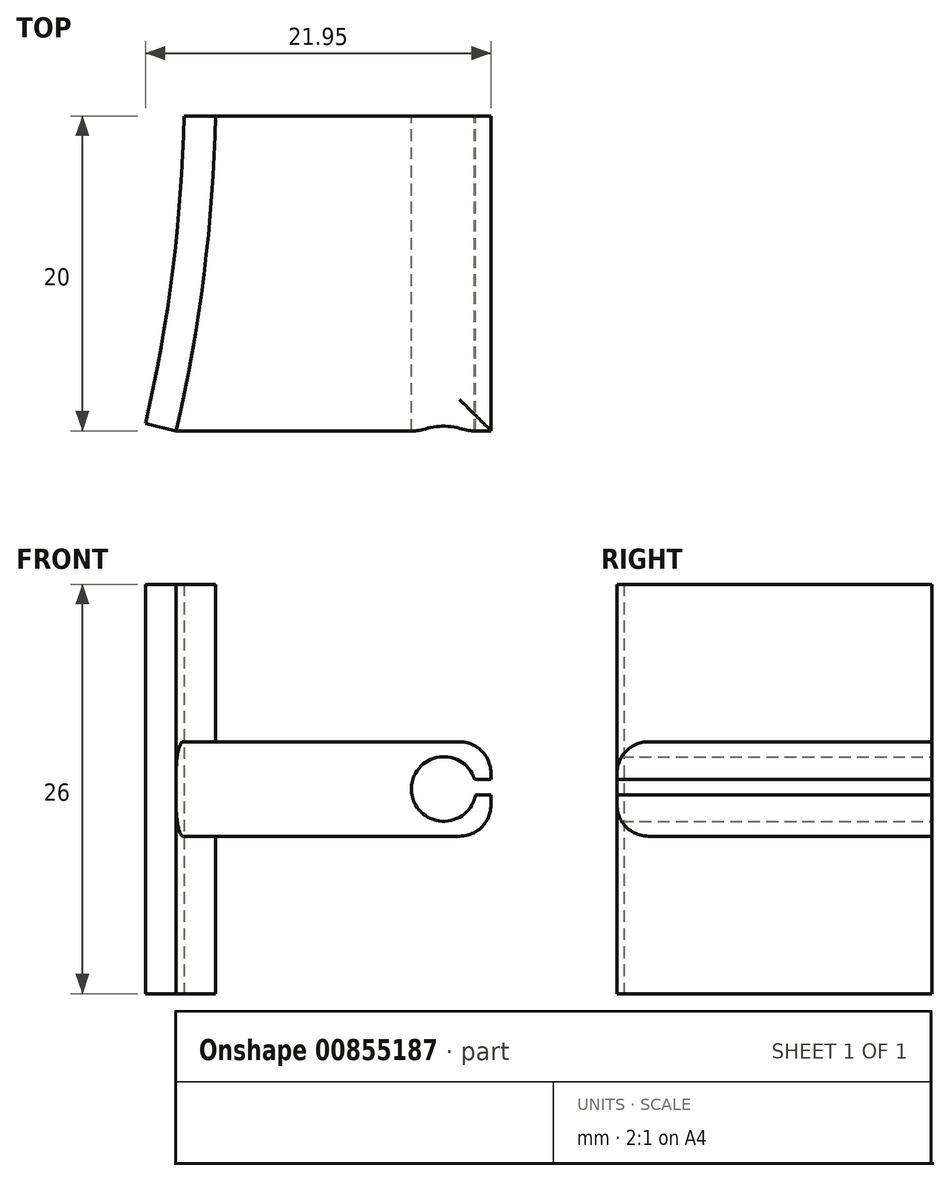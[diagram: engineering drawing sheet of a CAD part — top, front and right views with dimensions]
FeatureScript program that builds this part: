
annotation { "Feature Type Name" : "Feature", "Feature Type Description" : "" }
export const myFeature = defineFeature(function(context is Context, id is Id, definition is map)
    precondition{}
    {
        {
            var Q0;
            Q0=qCreatedBy(makeId("Top.planeOp"),FACE);
            var sketch = newSketch(context, id + "F0", { "sketchPlane" : qUnion([Q0])});
            skLineSegment(sketch, "E0.bottom", {"start": v(10, 10) * mm, "end": v(-9.5, 10) * mm});
            skLineSegment(sketch, "E0.top", {"start": v(10, -10) * mm, "end": v(-10, -10) * mm});
            skLineSegment(sketch, "E0.left", {"start": v(10, 10) * mm, "end": v(10, -10) * mm});
            skPoint(sketch, "E0.middle", {"position": v(0, 0) * mm});
            skArc(sketch, "E1", {"start": v(-10, -10) * mm, "mid": v(-8.23, -0.07) * mm, "end": v(-7.5, 10) * mm});
            skArc(sketch, "E2.0", {"start": v(-11.95, -9.55) * mm, "mid": v(-10.21, 0.18) * mm, "end": v(-9.5, 10.04) * mm});
            skPoint(sketch, "E3.orphan", {"position": v(-10, 10) * mm});
            skLineSegment(sketch, "E4", {"start": v(-11.95, -9.55) * mm, "end": v(-10, -10) * mm});
            skSolve(sketch);
        }
        {
            var Q0;
            {var subQ3=sQuery(id+"F0.wireOp",EDGE,"E1");Q0=makeQuery(id+"F0.imprint","IMPRINT",FACE,{"disambiguationData":[TD([[makeQuery(id+"F0.imprint","IMPRINT",EDGE,{"derivedFrom":subQ3}),1.0]])]});}
            extrude(context, id + "F1", {"entities" : qUnion([Q0]), "depth" : 16 * mm, "offsetDistance" : 25 * mm, "hasSecondDirection" : true, "secondDirectionOppositeDirection" : true, "secondDirectionDepth" : 10 * mm});
        }
        {
            var Q0;
            Q0=makeQuery(id+"F0.imprint","IMPRINT",FACE,{"disambiguationData":[TD([[makeQuery(id+"F0.imprint","IMPRINT",EDGE,{"derivedFrom":sQuery(id+"F0.wireOp",EDGE,"E0.top")}),-1.0]])]});
            extrude(context, id + "F2", {"entities" : qUnion([Q0]), "operationType" : NewBodyOperationType.ADD, "depth" : 6 * mm, "offsetDistance" : 25 * mm});
        }
        {
            var Q0;
            {var subQ0=sQuery(id+"F0.wireOp",EDGE,"E0.bottom");Q0=makeQuery(id+"F2.boolean.opBoolean","MERGE",FACE,{"derivedFrom":[makeQuery(id+"F1.opExtrude","SWEPT_FACE",FACE,{"disambiguationData":[OSD([subQ0])]}),makeQuery(id+"F2.opExtrude","SWEPT_FACE",FACE,{"disambiguationData":[OSD([subQ0])]})]});}
            var sketch = newSketch(context, id + "F3", { "sketchPlane" : qUnion([Q0])});
            skCircle(sketch, "E5", {"center": v(-7, 3) * mm, "radius": 2.05 * mm});
            skPoint(sketch, "E5.centerSnap0", {"position": v(-10, 3) * mm});
            skLineSegment(sketch, "E6", {"start": v(-10, 3.62) * mm, "end": v(-8.96, 3.62) * mm});
            skLineSegment(sketch, "E7", {"start": v(-10, 2.62) * mm, "end": v(-9.01, 2.62) * mm});
            skLineSegment(sketch, "E8", {"start": v(-10, 2.62) * mm, "end": v(-10, 3.62) * mm});
            skSolve(sketch);
        }
        {
            var Q0;
            {var subQ0=sQuery(id+"F3.wireOp",EDGE,"E5");var subQ1=makeQuery(id+"F3.imprint","INTERSECT",VERTEX,{"derivedFrom":[subQ0,sQuery(id+"F3.wireOp",EDGE,"E6")]});Q0=makeQuery(id+"F3.imprint","IMPRINT",FACE,{"disambiguationData":[TD([[makeQuery(id+"F3.imprint","IMPRINT",EDGE,{"disambiguationData":[TD([[subQ1,-1.0]])],"derivedFrom":subQ0}),1.0]])]});}
            var Q1;
            {var subQ0=sQuery(id+"F3.wireOp",EDGE,"E6");Q1=makeQuery(id+"F3.imprint","IMPRINT",FACE,{"disambiguationData":[TD([[makeQuery(id+"F3.imprint","IMPRINT",EDGE,{"derivedFrom":subQ0}),-1.0]])]});}
            extrude(context, id + "F4", {"entities" : qUnion([Q0, Q1]), "operationType" : NewBodyOperationType.REMOVE, "oppositeDirection" : true, "depth" : 25 * mm, "offsetDistance" : 25 * mm});
        }
        {
            var Q0;
            Q0=makeQuery(id+"F2.opExtrude","CAP_EDGE",EDGE,{"disambiguationData":[OSD([sQuery(id+"F0.wireOp",EDGE,"E0.top")])],"isStart":false});
            var Q1;
            Q1=makeQuery(id+"F2.opExtrude","CAP_EDGE",EDGE,{"disambiguationData":[OSD([sQuery(id+"F0.wireOp",EDGE,"E0.top")])],"isStart":true});
            var Q2;
            Q2=makeQuery(id+"F2.opExtrude","CAP_EDGE",EDGE,{"disambiguationData":[OSD([sQuery(id+"F0.wireOp",EDGE,"E0.left")])],"isStart":false});
            var Q3;
            Q3=makeQuery(id+"F2.opExtrude","CAP_EDGE",EDGE,{"disambiguationData":[OSD([sQuery(id+"F0.wireOp",EDGE,"E0.left")])],"isStart":true});
            fillet(context, id + "F5", {"entities" : qUnion([Q0, Q1, Q2, Q3]), "radius" : 2 * mm, "tangentPropagation" : true, "allowEdgeOverflow" : false});
        }
    });
